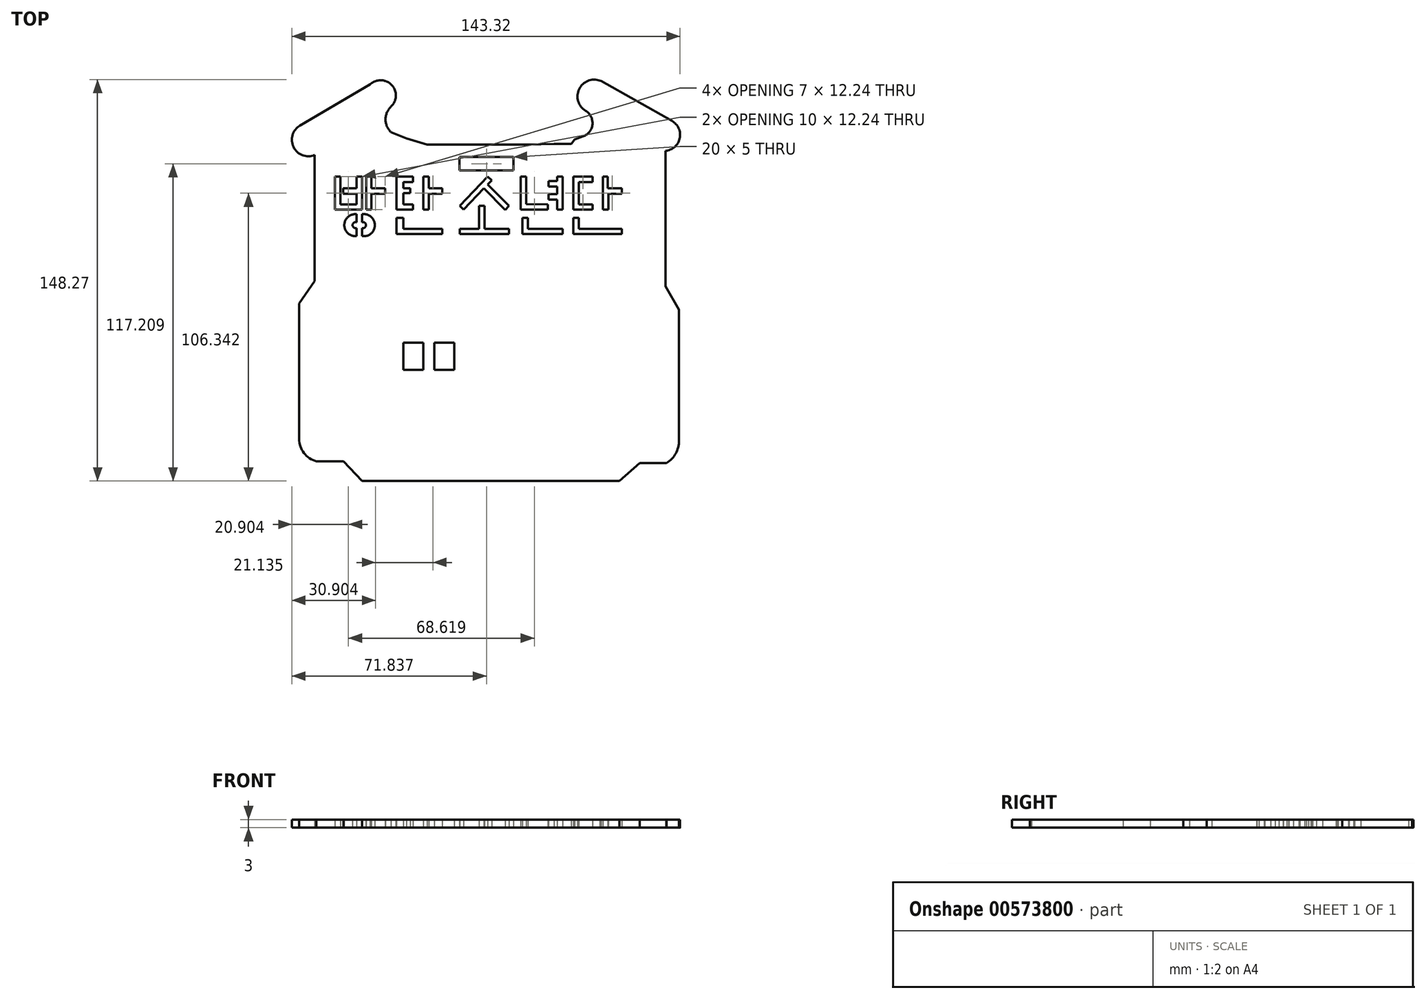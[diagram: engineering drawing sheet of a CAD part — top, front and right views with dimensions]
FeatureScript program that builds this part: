
annotation { "Feature Type Name" : "Feature", "Feature Type Description" : "" }
export const myFeature = defineFeature(function(context is Context, id is Id, definition is map)
    precondition{}
    {
        {
            var Q0;
            Q0=qCreatedBy(makeId("Top.planeOp"),FACE);
            var sketch = newSketch(context, id + "F0", { "sketchPlane" : qUnion([Q0])});
            skArc(sketch, "E0", {"start": v(-28.94, 36.71) * mm, "mid": v(-31, 31.95) * mm, "end": v(-28.94, 27.2) * mm});
            skLineSegment(sketch, "E1", {"start": v(-28.94, 27.2) * mm, "end": v(-23.32, 24.96) * mm});
            skLineSegment(sketch, "E2", {"start": v(-23.32, 24.96) * mm, "end": v(-15.65, 22.69) * mm});
            skLineSegment(sketch, "E3", {"start": v(-15.65, 22.69) * mm, "end": v(-9.1, 22.69) * mm});
            skLineSegment(sketch, "E4", {"start": v(-9.1, 22.69) * mm, "end": v(21.6, 22.69) * mm});
            skLineSegment(sketch, "E5", {"start": v(21.6, 22.69) * mm, "end": v(31.26, 22.97) * mm});
            skPoint(sketch, "E6.start.orphan", {"position": v(33.82, 22.97) * mm});
            skLineSegment(sketch, "E7", {"start": v(31.26, 22.97) * mm, "end": v(37.51, 22.97) * mm});
            skPoint(sketch, "E8.start.orphan", {"position": v(39.5, 22.97) * mm});
            skLineSegment(sketch, "E9", {"start": v(38.85, 24.6) * mm, "end": v(41.9, 25.68) * mm});
            skArc(sketch, "E10", {"start": v(41.9, 25.68) * mm, "mid": v(45.38, 30.12) * mm, "end": v(42.85, 35.16) * mm});
            skArc(sketch, "E11", {"start": v(42.85, 35.16) * mm, "mid": v(40.46, 43.13) * mm, "end": v(48.16, 46.3) * mm});
            skLineSegment(sketch, "E12", {"start": v(48.65, 46.17) * mm, "end": v(74.75, 31.38) * mm});
            skArc(sketch, "E13", {"start": v(74.75, 31.38) * mm, "mid": v(77.6, 25) * mm, "end": v(72.35, 20.37) * mm});
            skLineSegment(sketch, "E14", {"start": v(72.35, 20.37) * mm, "end": v(72.35, -29.63) * mm});
            skLineSegment(sketch, "E15", {"start": v(72.35, -29.63) * mm, "end": v(77.36, -38.28) * mm});
            skLineSegment(sketch, "E16", {"start": v(77.36, -38.28) * mm, "end": v(77.36, -86.63) * mm});
            skPoint(sketch, "E17.start.orphan", {"position": v(-28.94, 36.71) * mm});
            skArc(sketch, "E18", {"start": v(-28.94, 36.71) * mm, "mid": v(-28.72, 44.7) * mm, "end": v(-36.7, 44.86) * mm});
            skLineSegment(sketch, "E19", {"start": v(-36.7, 44.86) * mm, "end": v(-62.58, 29.68) * mm});
            skArc(sketch, "E20", {"start": v(-62.58, 29.68) * mm, "mid": v(-64.94, 21.72) * mm, "end": v(-57.16, 18.84) * mm});
            skLineSegment(sketch, "E21", {"start": v(-57.16, 18.84) * mm, "end": v(-57.16, -27.8) * mm});
            skLineSegment(sketch, "E22", {"start": v(-57.16, -27.8) * mm, "end": v(-62.87, -36) * mm});
            skLineSegment(sketch, "E23", {"start": v(-62.87, -36) * mm, "end": v(-62.87, -86) * mm});
            skArc(sketch, "E24", {"start": v(-62.87, -86) * mm, "mid": v(-61.1, -91.23) * mm, "end": v(-56.52, -94.3) * mm});
            skArc(sketch, "E25", {"start": v(77.36, -86.63) * mm, "mid": v(76.14, -91.37) * mm, "end": v(72.77, -94.93) * mm});
            skLineSegment(sketch, "E26", {"start": v(-56.52, -94.3) * mm, "end": v(-46.52, -94.3) * mm});
            skLineSegment(sketch, "E27", {"start": v(72.77, -94.93) * mm, "end": v(62.77, -94.93) * mm});
            skLineSegment(sketch, "E28", {"start": v(-46.52, -94.3) * mm, "end": v(-39.68, -101.6) * mm});
            skLineSegment(sketch, "E29", {"start": v(-39.68, -101.6) * mm, "end": v(55.32, -101.6) * mm});
            skLineSegment(sketch, "E30", {"start": v(62.77, -94.93) * mm, "end": v(55.32, -101.6) * mm});
            skLineSegment(sketch, "E31", {"start": v(-3.74, 18.1) * mm, "end": v(16.26, 18.1) * mm});
            skLineSegment(sketch, "E32", {"start": v(-3.74, 18.1) * mm, "end": v(-3.74, 13.1) * mm});
            skLineSegment(sketch, "E33", {"start": v(-3.74, 13.1) * mm, "end": v(16.26, 13.1) * mm});
            skLineSegment(sketch, "E34", {"start": v(16.26, 13.1) * mm, "end": v(16.26, 18.1) * mm});
            skLineSegment(sketch, "E35", {"start": v(-57.16, 13.1) * mm, "end": v(-57.16, -11.9) * mm});
            skLineSegment(sketch, "E36", {"start": v(6.74, 10.86) * mm, "end": v(-3.6, 0) * mm});
            skLineSegment(sketch, "E37", {"start": v(-3.6, 0) * mm, "end": v(-2.15, -1.38) * mm});
            skLineSegment(sketch, "E38", {"start": v(-2.15, -1.38) * mm, "end": v(8.19, 9.48) * mm});
            skLineSegment(sketch, "E39", {"start": v(6.74, 10.86) * mm, "end": v(8.19, 9.48) * mm});
            skLineSegment(sketch, "E40", {"start": v(6.74, 7.96) * mm, "end": v(14.55, 0) * mm});
            skLineSegment(sketch, "E41", {"start": v(14.55, 0) * mm, "end": v(13.12, -1.4) * mm});
            skLineSegment(sketch, "E42", {"start": v(13.12, -1.4) * mm, "end": v(5.36, 6.51) * mm});
            skLineSegment(sketch, "E43", {"start": v(2.83, -8.4) * mm, "end": v(-3.6, -8.4) * mm});
            skLineSegment(sketch, "E44", {"start": v(-3.6, -8.4) * mm, "end": v(-3.6, -10.4) * mm});
            skLineSegment(sketch, "E45", {"start": v(-3.6, -10.4) * mm, "end": v(14.55, -10.4) * mm});
            skLineSegment(sketch, "E46", {"start": v(14.55, -10.4) * mm, "end": v(14.55, -8.4) * mm});
            skLineSegment(sketch, "E47", {"start": v(14.55, -8.4) * mm, "end": v(-3.6, -8.4) * mm});
            skPoint(sketch, "E48.start.orphan", {"position": v(3.52, 0) * mm});
            skLineSegment(sketch, "E49", {"start": v(3.52, 0) * mm, "end": v(3.52, -8.4) * mm});
            skLineSegment(sketch, "E50", {"start": v(3.52, 0) * mm, "end": v(5.52, 0) * mm});
            skLineSegment(sketch, "E51", {"start": v(5.52, 0) * mm, "end": v(5.52, -8.4) * mm});
            skPoint(sketch, "E52.end.orphan", {"position": v(4.72, -8.4) * mm});
            skLineSegment(sketch, "E53", {"start": v(4.72, -8.4) * mm, "end": v(5.52, -8.4) * mm});
            skLineSegment(sketch, "E54", {"start": v(-15.04, 10.86) * mm, "end": v(-15.04, -1.38) * mm});
            skLineSegment(sketch, "E55", {"start": v(-15.04, 10.86) * mm, "end": v(-17.04, 10.86) * mm});
            skLineSegment(sketch, "E56", {"start": v(-15.04, -1.38) * mm, "end": v(-17.04, -1.38) * mm});
            skLineSegment(sketch, "E57", {"start": v(-17.04, -1.38) * mm, "end": v(-17.04, 10.86) * mm});
            skLineSegment(sketch, "E58", {"start": v(-15.04, 6.51) * mm, "end": v(-10.04, 6.51) * mm});
            skLineSegment(sketch, "E59", {"start": v(-10.04, 4.51) * mm, "end": v(-10.04, 6.51) * mm});
            skLineSegment(sketch, "E60", {"start": v(-10.04, 4.51) * mm, "end": v(-15.04, 4.51) * mm});
            skPoint(sketch, "E60.endSnap0", {"position": v(-15.04, 4.74) * mm});
            skLineSegment(sketch, "E61", {"start": v(-20.92, 10.86) * mm, "end": v(-26.92, 10.86) * mm});
            skLineSegment(sketch, "E62", {"start": v(-26.92, -1.38) * mm, "end": v(-26.92, 10.86) * mm});
            skLineSegment(sketch, "E63", {"start": v(-26.92, -1.38) * mm, "end": v(-20.92, -1.38) * mm});
            skLineSegment(sketch, "E64", {"start": v(-20.92, -1.38) * mm, "end": v(-20.92, 0.62) * mm});
            skLineSegment(sketch, "E65", {"start": v(-20.92, 10.86) * mm, "end": v(-20.92, 8.86) * mm});
            skLineSegment(sketch, "E66", {"start": v(-24.42, 8.86) * mm, "end": v(-20.92, 8.86) * mm});
            skLineSegment(sketch, "E67", {"start": v(-20.92, 0.62) * mm, "end": v(-24.42, 0.62) * mm});
            skLineSegment(sketch, "E68", {"start": v(-24.42, 0.62) * mm, "end": v(-24.42, 4.74) * mm});
            skPoint(sketch, "E68.endSnap0", {"position": v(-17.04, 4.74) * mm});
            skLineSegment(sketch, "E69", {"start": v(-24.42, 4.74) * mm, "end": v(-21.92, 4.74) * mm});
            skLineSegment(sketch, "E70", {"start": v(-21.92, 4.74) * mm, "end": v(-21.92, 6.51) * mm});
            skLineSegment(sketch, "E71", {"start": v(-21.92, 6.51) * mm, "end": v(-24.42, 6.51) * mm});
            skLineSegment(sketch, "E72", {"start": v(-24.42, 6.51) * mm, "end": v(-24.42, 8.86) * mm});
            skLineSegment(sketch, "E73", {"start": v(-26.92, -10.4) * mm, "end": v(-26.92, -4.4) * mm});
            skLineSegment(sketch, "E74", {"start": v(-26.92, -4.4) * mm, "end": v(-24.42, -4.4) * mm});
            skLineSegment(sketch, "E75", {"start": v(-24.42, -4.4) * mm, "end": v(-24.42, -8.4) * mm});
            skLineSegment(sketch, "E76", {"start": v(-24.42, -8.4) * mm, "end": v(-10.04, -8.4) * mm});
            skLineSegment(sketch, "E77", {"start": v(-10.04, -8.4) * mm, "end": v(-10.04, -10.4) * mm});
            skLineSegment(sketch, "E78", {"start": v(-26.92, -10.4) * mm, "end": v(-10.04, -10.4) * mm});
            skLineSegment(sketch, "E79", {"start": v(-36.18, 10.86) * mm, "end": v(-36.18, 6.51) * mm});
            skLineSegment(sketch, "E80", {"start": v(-36.18, 6.51) * mm, "end": v(-31.18, 6.51) * mm});
            skPoint(sketch, "E80.endSnap0", {"position": v(-23.17, 6.51) * mm});
            skLineSegment(sketch, "E81", {"start": v(-36.18, 4.51) * mm, "end": v(-33.38, 4.51) * mm});
            skLineSegment(sketch, "E82", {"start": v(-31.18, 6.51) * mm, "end": v(-31.18, 4.51) * mm});
            skLineSegment(sketch, "E83", {"start": v(-33.38, 4.51) * mm, "end": v(-31.18, 4.51) * mm});
            skLineSegment(sketch, "E84", {"start": v(-36.18, 4.51) * mm, "end": v(-36.18, -1.38) * mm});
            skLineSegment(sketch, "E85", {"start": v(-36.18, -1.38) * mm, "end": v(-38.18, -1.38) * mm});
            skLineSegment(sketch, "E86", {"start": v(-38.18, -1.38) * mm, "end": v(-38.18, 10.86) * mm});
            skLineSegment(sketch, "E87", {"start": v(-38.18, 10.86) * mm, "end": v(-36.18, 10.86) * mm});
            skLineSegment(sketch, "E88", {"start": v(-39.68, 10.86) * mm, "end": v(-39.68, -1.38) * mm});
            skLineSegment(sketch, "E89", {"start": v(-39.68, -1.38) * mm, "end": v(-49.68, -1.38) * mm});
            skLineSegment(sketch, "E90", {"start": v(-49.68, 10.86) * mm, "end": v(-49.68, -1.38) * mm});
            skLineSegment(sketch, "E91", {"start": v(-49.68, 10.86) * mm, "end": v(-47.68, 10.86) * mm});
            skLineSegment(sketch, "E92", {"start": v(-47.68, 0.62) * mm, "end": v(-47.68, 10.86) * mm});
            skLineSegment(sketch, "E93", {"start": v(-39.68, 10.86) * mm, "end": v(-41.68, 10.86) * mm});
            skLineSegment(sketch, "E94", {"start": v(-41.68, 6.51) * mm, "end": v(-41.68, 10.86) * mm});
            skLineSegment(sketch, "E95", {"start": v(-41.68, 6.51) * mm, "end": v(-46.68, 6.51) * mm});
            skLineSegment(sketch, "E96", {"start": v(-46.68, 4.51) * mm, "end": v(-41.68, 4.51) * mm});
            skLineSegment(sketch, "E97", {"start": v(-41.68, 4.51) * mm, "end": v(-41.68, 0.62) * mm});
            skLineSegment(sketch, "E98", {"start": v(-47.68, 0.62) * mm, "end": v(-41.68, 0.62) * mm});
            skLineSegment(sketch, "E99", {"start": v(-46.68, 6.51) * mm, "end": v(-46.68, 4.51) * mm});
            skLineSegment(sketch, "E100", {"start": v(18.94, 10.86) * mm, "end": v(18.94, -1.38) * mm});
            skLineSegment(sketch, "E101", {"start": v(18.94, -1.38) * mm, "end": v(28.94, -1.38) * mm});
            skLineSegment(sketch, "E102", {"start": v(28.94, -1.38) * mm, "end": v(28.94, 0.62) * mm});
            skLineSegment(sketch, "E103", {"start": v(18.94, 10.86) * mm, "end": v(20.94, 10.86) * mm});
            skLineSegment(sketch, "E104", {"start": v(20.94, 0.62) * mm, "end": v(20.94, 10.86) * mm});
            skLineSegment(sketch, "E105", {"start": v(20.75, 0.75) * mm, "end": v(28.94, 0.62) * mm});
            skLineSegment(sketch, "E106", {"start": v(34.35, 10.86) * mm, "end": v(34.35, -1.38) * mm});
            skLineSegment(sketch, "E107", {"start": v(34.35, -1.38) * mm, "end": v(32.35, -1.38) * mm});
            skLineSegment(sketch, "E108", {"start": v(32.35, -1.38) * mm, "end": v(32.35, 2.37) * mm});
            skLineSegment(sketch, "E109", {"start": v(32.35, 2.37) * mm, "end": v(29.24, 2.37) * mm});
            skLineSegment(sketch, "E110", {"start": v(29.24, 2.37) * mm, "end": v(29.24, 4.37) * mm});
            skLineSegment(sketch, "E111", {"start": v(29.24, 4.37) * mm, "end": v(32.35, 4.37) * mm});
            skLineSegment(sketch, "E112", {"start": v(32.35, 4.37) * mm, "end": v(32.35, 7.17) * mm});
            skLineSegment(sketch, "E113", {"start": v(32.35, 7.17) * mm, "end": v(29.24, 7.17) * mm});
            skLineSegment(sketch, "E114", {"start": v(29.24, 7.17) * mm, "end": v(29.24, 9.17) * mm});
            skLineSegment(sketch, "E115", {"start": v(29.24, 9.17) * mm, "end": v(32.35, 9.17) * mm});
            skLineSegment(sketch, "E116", {"start": v(32.35, 9.17) * mm, "end": v(32.35, 10.86) * mm});
            skLineSegment(sketch, "E117", {"start": v(32.35, 10.86) * mm, "end": v(34.35, 10.86) * mm});
            skLineSegment(sketch, "E118", {"start": v(19.56, -4.4) * mm, "end": v(19.56, -10.4) * mm});
            skLineSegment(sketch, "E119", {"start": v(19.56, -10.4) * mm, "end": v(34.35, -10.4) * mm});
            skLineSegment(sketch, "E120", {"start": v(34.35, -10.4) * mm, "end": v(34.35, -8.4) * mm});
            skLineSegment(sketch, "E121", {"start": v(19.56, -4.4) * mm, "end": v(21.56, -4.4) * mm});
            skLineSegment(sketch, "E122", {"start": v(21.56, -4.4) * mm, "end": v(21.56, -8.4) * mm});
            skLineSegment(sketch, "E123", {"start": v(21.56, -8.4) * mm, "end": v(34.35, -8.4) * mm});
            skLineSegment(sketch, "E124", {"start": v(38.38, 10.86) * mm, "end": v(45.38, 10.86) * mm});
            skLineSegment(sketch, "E125", {"start": v(45.38, 10.86) * mm, "end": v(45.38, 8.86) * mm});
            skLineSegment(sketch, "E126", {"start": v(45.38, 8.86) * mm, "end": v(40.38, 8.86) * mm});
            skLineSegment(sketch, "E127", {"start": v(38.38, 10.86) * mm, "end": v(38.38, -1.38) * mm});
            skLineSegment(sketch, "E128", {"start": v(38.38, -1.38) * mm, "end": v(45.38, -1.38) * mm});
            skLineSegment(sketch, "E129", {"start": v(45.38, -1.38) * mm, "end": v(45.38, 0.62) * mm});
            skLineSegment(sketch, "E130", {"start": v(45.38, 0.62) * mm, "end": v(40.38, 0.62) * mm});
            skLineSegment(sketch, "E131", {"start": v(40.38, 0.62) * mm, "end": v(40.38, 8.86) * mm});
            skLineSegment(sketch, "E132", {"start": v(49.22, 10.86) * mm, "end": v(49.22, -1.38) * mm});
            skLineSegment(sketch, "E133", {"start": v(49.22, -1.38) * mm, "end": v(51.22, -1.38) * mm});
            skLineSegment(sketch, "E134", {"start": v(51.22, -1.38) * mm, "end": v(51.22, 4.51) * mm});
            skLineSegment(sketch, "E135", {"start": v(51.22, 4.51) * mm, "end": v(56.22, 4.51) * mm});
            skLineSegment(sketch, "E136", {"start": v(56.22, 4.51) * mm, "end": v(56.22, 6.51) * mm});
            skLineSegment(sketch, "E137", {"start": v(56.22, 6.51) * mm, "end": v(50.96, 6.51) * mm});
            skLineSegment(sketch, "E138", {"start": v(50.96, 6.51) * mm, "end": v(50.96, 10.86) * mm});
            skLineSegment(sketch, "E139", {"start": v(50.96, 10.86) * mm, "end": v(49.22, 10.86) * mm});
            skLineSegment(sketch, "E140", {"start": v(38.38, -4.4) * mm, "end": v(38.38, -10.4) * mm});
            skLineSegment(sketch, "E141", {"start": v(38.38, -10.4) * mm, "end": v(56.22, -10.4) * mm});
            skLineSegment(sketch, "E142", {"start": v(56.22, -10.4) * mm, "end": v(56.22, -8.4) * mm});
            skLineSegment(sketch, "E143", {"start": v(56.22, -8.4) * mm, "end": v(40.38, -8.4) * mm});
            skLineSegment(sketch, "E144", {"start": v(40.38, -8.4) * mm, "end": v(40.38, -4.4) * mm});
            skLineSegment(sketch, "E145", {"start": v(40.38, -4.4) * mm, "end": v(38.38, -4.4) * mm});
            skLineSegment(sketch, "E146", {"start": v(-57.16, -23.34) * mm, "end": v(72.35, -23.34) * mm});
            skLineSegment(sketch, "E147", {"start": v(-33.38, -44.48) * mm, "end": v(-49.9, -44.48) * mm});
            skLineSegment(sketch, "E148", {"start": v(-49.9, -44.48) * mm, "end": v(-49.9, -46.48) * mm});
            skLineSegment(sketch, "E149", {"start": v(-49.9, -46.48) * mm, "end": v(-33.38, -46.48) * mm});
            skLineSegment(sketch, "E150", {"start": v(-33.38, -46.48) * mm, "end": v(-33.38, -44.48) * mm});
            skLineSegment(sketch, "E151", {"start": v(-47.9, -46.48) * mm, "end": v(-47.9, -50.48) * mm});
            skLineSegment(sketch, "E152", {"start": v(-47.9, -50.48) * mm, "end": v(-34.96, -50.48) * mm});
            skLineSegment(sketch, "E153", {"start": v(-34.96, -50.48) * mm, "end": v(-34.96, -46.48) * mm});
            skLineSegment(sketch, "E154", {"start": v(-47.9, -50.48) * mm, "end": v(-49.9, -50.48) * mm});
            skLineSegment(sketch, "E155", {"start": v(-49.9, -50.48) * mm, "end": v(-49.9, -60.48) * mm});
            skLineSegment(sketch, "E156", {"start": v(-49.9, -60.48) * mm, "end": v(-33.38, -60.48) * mm});
            skLineSegment(sketch, "E157", {"start": v(-33.38, -60.48) * mm, "end": v(-33.38, -50.48) * mm});
            skLineSegment(sketch, "E158", {"start": v(-33.38, -50.48) * mm, "end": v(-34.96, -50.48) * mm});
            skLineSegment(sketch, "E159", {"start": v(-47.9, -60.48) * mm, "end": v(-47.9, -64.48) * mm});
            skLineSegment(sketch, "E160", {"start": v(-47.9, -64.48) * mm, "end": v(-34.96, -64.48) * mm});
            skLineSegment(sketch, "E161", {"start": v(-34.96, -64.48) * mm, "end": v(-34.96, -60.48) * mm});
            skLineSegment(sketch, "E162", {"start": v(-47.9, -64.48) * mm, "end": v(-49.9, -64.48) * mm});
            skLineSegment(sketch, "E163", {"start": v(-34.96, -64.48) * mm, "end": v(-33.38, -64.48) * mm});
            skLineSegment(sketch, "E164", {"start": v(-33.38, -64.48) * mm, "end": v(-33.38, -66.48) * mm});
            skLineSegment(sketch, "E165", {"start": v(-33.38, -66.48) * mm, "end": v(-49.9, -66.48) * mm});
            skLineSegment(sketch, "E166", {"start": v(-49.9, -66.48) * mm, "end": v(-49.9, -64.48) * mm});
            skLineSegment(sketch, "E167", {"start": v(-45.95, -44.48) * mm, "end": v(-45.95, -42.48) * mm});
            skLineSegment(sketch, "E168", {"start": v(-41.95, -42.48) * mm, "end": v(-45.95, -42.48) * mm});
            skLineSegment(sketch, "E169", {"start": v(-41.95, -44.48) * mm, "end": v(-41.95, -42.48) * mm});
            skLineSegment(sketch, "E170", {"start": v(-41.95, -42.48) * mm, "end": v(-37.95, -42.48) * mm});
            skLineSegment(sketch, "E171", {"start": v(-37.95, -42.48) * mm, "end": v(-37.95, -44.48) * mm});
            skLineSegment(sketch, "E172", {"start": v(-45.95, -42.48) * mm, "end": v(-47.4, -42.48) * mm});
            skLineSegment(sketch, "E173", {"start": v(-47.4, -42.48) * mm, "end": v(-47.4, -40.48) * mm});
            skLineSegment(sketch, "E174", {"start": v(-47.4, -40.48) * mm, "end": v(-34.96, -40.48) * mm});
            skLineSegment(sketch, "E175", {"start": v(-37.95, -42.48) * mm, "end": v(-34.96, -42.48) * mm});
            skLineSegment(sketch, "E176", {"start": v(-34.96, -42.48) * mm, "end": v(-33.38, -44.48) * mm});
            skLineSegment(sketch, "E177", {"start": v(-33.38, -46.48) * mm, "end": v(-33.38, -48.48) * mm});
            skPoint(sketch, "E177.endSnap0", {"position": v(-34.96, -48.48) * mm});
            skLineSegment(sketch, "E178", {"start": v(-33.38, -48.48) * mm, "end": v(-31.38, -48.48) * mm});
            skLineSegment(sketch, "E179", {"start": v(-31.38, -48.48) * mm, "end": v(-31.38, -44.48) * mm});
            skLineSegment(sketch, "E180", {"start": v(-31.38, -44.48) * mm, "end": v(-34.96, -40.48) * mm});
            skLineSegment(sketch, "E181.bottom", {"start": v(-24.42, -50.48) * mm, "end": v(-17.03, -50.48) * mm});
            skLineSegment(sketch, "E181.top", {"start": v(-24.42, -60.48) * mm, "end": v(-17.03, -60.48) * mm});
            skLineSegment(sketch, "E181.left", {"start": v(-24.42, -50.48) * mm, "end": v(-24.42, -60.48) * mm});
            skLineSegment(sketch, "E181.right", {"start": v(-17.03, -50.48) * mm, "end": v(-17.03, -60.48) * mm});
            skLineSegment(sketch, "E182.bottom", {"start": v(-12.99, -50.48) * mm, "end": v(-5.6, -50.48) * mm});
            skLineSegment(sketch, "E182.top", {"start": v(-12.99, -60.48) * mm, "end": v(-5.6, -60.48) * mm});
            skLineSegment(sketch, "E182.left", {"start": v(-12.99, -50.48) * mm, "end": v(-12.99, -60.48) * mm});
            skLineSegment(sketch, "E182.right", {"start": v(-5.6, -50.48) * mm, "end": v(-5.6, -60.48) * mm});
            skLineSegment(sketch, "E183", {"start": v(23.94, -36) * mm, "end": v(33.94, -36.16) * mm});
            skPoint(sketch, "E183.startSnap0", {"position": v(23.94, -1.38) * mm});
            skPoint(sketch, "E184.endSnap0", {"position": v(-34.96, -62.48) * mm});
            skLineSegment(sketch, "E185", {"start": v(23.94, -36) * mm, "end": v(23.94, -64.48) * mm});
            skLineSegment(sketch, "E186", {"start": v(33.94, -36.16) * mm, "end": v(33.94, -64.48) * mm});
            skLineSegment(sketch, "E187", {"start": v(38.38, -36.16) * mm, "end": v(48.38, -36.16) * mm});
            skLineSegment(sketch, "E188", {"start": v(48.38, -36.16) * mm, "end": v(48.38, -64.48) * mm});
            skLineSegment(sketch, "E189", {"start": v(38.38, -36.16) * mm, "end": v(38.38, -64.48) * mm});
            skArc(sketch, "E190", {"start": v(23.94, -64.48) * mm, "mid": v(28.94, -69.48) * mm, "end": v(33.94, -64.48) * mm});
            skArc(sketch, "E191", {"start": v(38.38, -64.48) * mm, "mid": v(43.38, -69.48) * mm, "end": v(48.38, -64.48) * mm});
            skPoint(sketch, "E192", {"position": v(28.94, -28.41) * mm});
            skPoint(sketch, "E193", {"position": v(43.38, -28.41) * mm});
            skPoint(sketch, "E194", {"position": v(12.42, -28.41) * mm});
            skLineSegment(sketch, "E195", {"start": v(37.51, 22.97) * mm, "end": v(38.85, 24.6) * mm});
            skLineSegment(sketch, "E196", {"start": v(48.16, 46.3) * mm, "end": v(48.65, 46.17) * mm});
            skLineSegment(sketch, "E197", {"start": v(-41.68, -3.03) * mm, "end": v(-41.68, -6.03) * mm});
            skLineSegment(sketch, "E198", {"start": v(-41.68, -11.13) * mm, "end": v(-41.68, -8.13) * mm});
            skArc(sketch, "E199", {"start": v(-41.68, -3.03) * mm, "mid": v(-46.21, -7.08) * mm, "end": v(-41.68, -11.13) * mm});
            skArc(sketch, "E200", {"start": v(-41.68, -6.03) * mm, "mid": v(-43.17, -7.08) * mm, "end": v(-41.68, -8.13) * mm});
            skLineSegment(sketch, "E201", {"start": v(-39.68, -3.03) * mm, "end": v(-39.68, -6.03) * mm});
            skLineSegment(sketch, "E202", {"start": v(-39.68, -8.13) * mm, "end": v(-39.68, -11.13) * mm});
            skArc(sketch, "E203", {"start": v(-39.68, -11.13) * mm, "mid": v(-34.94, -7.08) * mm, "end": v(-39.68, -3.03) * mm});
            skArc(sketch, "E204", {"start": v(-39.68, -8.13) * mm, "mid": v(-38.2, -7.08) * mm, "end": v(-39.68, -6.03) * mm});
            skSolve(sketch);
        }
        {
            var Q0;
            Q0=makeQuery(id+"F0.imprint","IMPRINT",FACE,{"disambiguationData":[TD([[makeQuery(id+"F0.imprint","IMPRINT",EDGE,{"derivedFrom":sQuery(id+"F0.wireOp",EDGE,"E152")}),-1.0]])]});
            var Q1;
            {var subQ9=sQuery(id+"F0.wireOp",EDGE,"E15");Q1=makeQuery(id+"F0.imprint","IMPRINT",FACE,{"disambiguationData":[TD([[makeQuery(id+"F0.imprint","IMPRINT",EDGE,{"derivedFrom":subQ9}),-1.0]])]});}
            var Q2;
            {var subQ0=sQuery(id+"F0.wireOp",EDGE,"E151");Q2=makeQuery(id+"F0.imprint","IMPRINT",FACE,{"disambiguationData":[TD([[makeQuery(id+"F0.imprint","IMPRINT",EDGE,{"derivedFrom":subQ0}),1.0]])]});}
            var Q3;
            Q3=makeQuery(id+"F0.imprint","IMPRINT",FACE,{"disambiguationData":[TD([[makeQuery(id+"F0.imprint","IMPRINT",EDGE,{"derivedFrom":sQuery(id+"F0.wireOp",EDGE,"E183")}),-1.0]])]});
            var Q4;
            Q4=makeQuery(id+"F0.imprint","IMPRINT",FACE,{"disambiguationData":[TD([[makeQuery(id+"F0.imprint","IMPRINT",EDGE,{"derivedFrom":sQuery(id+"F0.wireOp",EDGE,"E187")}),-1.0]])]});
            var Q5;
            Q5=makeQuery(id+"F0.imprint","IMPRINT",FACE,{"disambiguationData":[TD([[makeQuery(id+"F0.imprint","IMPRINT",EDGE,{"derivedFrom":sQuery(id+"F0.wireOp",EDGE,"E0")}),-1.0]])]});
            var Q6;
            {var subQ0=sQuery(id+"F0.wireOp",EDGE,"E159");Q6=makeQuery(id+"F0.imprint","IMPRINT",FACE,{"disambiguationData":[TD([[makeQuery(id+"F0.imprint","IMPRINT",EDGE,{"derivedFrom":subQ0}),1.0]])]});}
            var Q7;
            Q7=makeQuery(id+"F0.imprint","IMPRINT",FACE,{"disambiguationData":[TD([[makeQuery(id+"F0.imprint","IMPRINT",EDGE,{"derivedFrom":sQuery(id+"F0.wireOp",EDGE,"E160")}),-1.0]])]});
            var Q8;
            {var subQ0=sQuery(id+"F0.wireOp",EDGE,"E148");Q8=makeQuery(id+"F0.imprint","IMPRINT",FACE,{"disambiguationData":[TD([[makeQuery(id+"F0.imprint","IMPRINT",EDGE,{"derivedFrom":subQ0}),1.0]])]});}
            var Q9;
            {var subQ0=sQuery(id+"F0.wireOp",EDGE,"E169");Q9=makeQuery(id+"F0.imprint","IMPRINT",FACE,{"disambiguationData":[TD([[makeQuery(id+"F0.imprint","IMPRINT",EDGE,{"derivedFrom":subQ0}),-1.0]])]});}
            var Q10;
            {var subQ2=sQuery(id+"F0.wireOp",EDGE,"E171");Q10=makeQuery(id+"F0.imprint","IMPRINT",FACE,{"disambiguationData":[TD([[makeQuery(id+"F0.imprint","IMPRINT",EDGE,{"derivedFrom":subQ2}),1.0]])]});}
            var Q11;
            {var subQ0=sQuery(id+"F0.wireOp",EDGE,"E167");Q11=makeQuery(id+"F0.imprint","IMPRINT",FACE,{"disambiguationData":[TD([[makeQuery(id+"F0.imprint","IMPRINT",EDGE,{"derivedFrom":subQ0}),-1.0]])]});}
            var Q12;
            Q12=makeQuery(id+"F0.imprint","IMPRINT",FACE,{"disambiguationData":[TD([[makeQuery(id+"F0.imprint","IMPRINT",EDGE,{"derivedFrom":sQuery(id+"F0.wireOp",EDGE,"E150")}),-1.0]])]});
            extrude(context, id + "F1", {"entities" : qUnion([Q0, Q1, Q2, Q3, Q4, Q5, Q6, Q7, Q8, Q9, Q10, Q11, Q12]), "depth" : 3 * mm, "offsetDistance" : 25 * mm});
        }
    });
